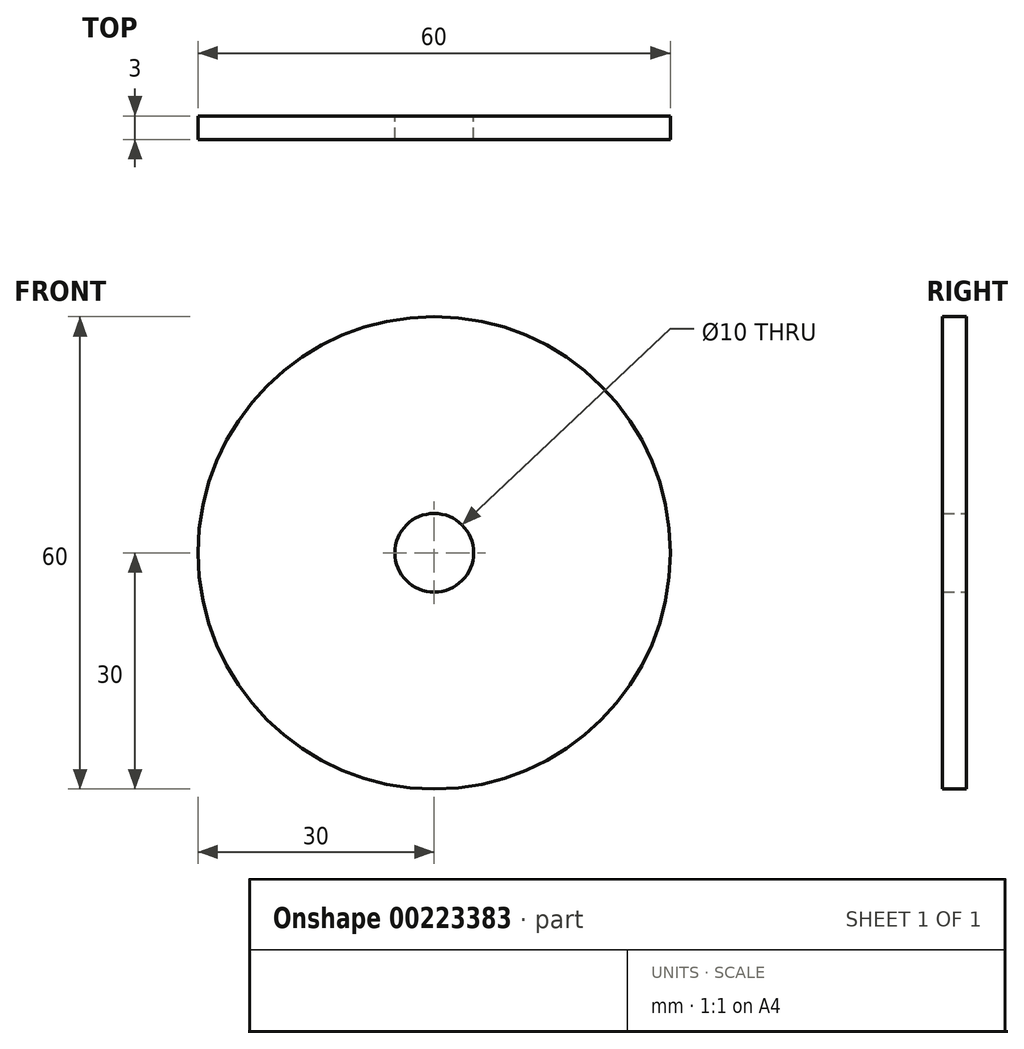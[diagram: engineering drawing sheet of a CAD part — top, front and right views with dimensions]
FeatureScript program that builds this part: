
annotation { "Feature Type Name" : "Feature", "Feature Type Description" : "" }
export const myFeature = defineFeature(function(context is Context, id is Id, definition is map)
    precondition{}
    {
        {
            var Q0;
            Q0=qCreatedBy(makeId("Front.planeOp"),FACE);
            var sketch = newSketch(context, id + "F0", { "sketchPlane" : qUnion([Q0])});
            skCircle(sketch, "E0", {"center": v(0, 0) * mm, "radius": 30 * mm});
            skCircle(sketch, "E1", {"center": v(0, 0) * mm, "radius": 5 * mm});
            skSolve(sketch);
        }
        {
            var Q0;
            Q0=makeQuery(id+"F0.imprint","IMPRINT",FACE,{"disambiguationData":[TD([[makeQuery(id+"F0.imprint","IMPRINT",EDGE,{"derivedFrom":sQuery(id+"F0.wireOp",EDGE,"E0")}),1.0]])]});
            extrude(context, id + "F1", {"entities" : qUnion([Q0]), "depth" : 3 * mm});
        }
    });
